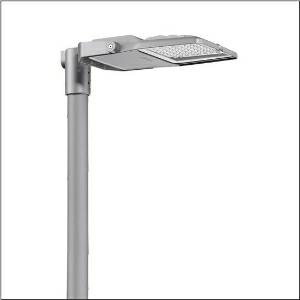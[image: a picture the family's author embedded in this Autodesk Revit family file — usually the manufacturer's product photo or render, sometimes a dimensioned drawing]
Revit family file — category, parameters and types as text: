
# Revit family: floodlight_fl_21_iq_mini___pl64_5xa7771c2e3a_b06c
name_source: partatom
category: Lighting Fixtures
units: mm (PartAtom-declared; Revit-internal decimal feet)

## family parameters
Cut with Voids When Loaded = No
Host = Face
Light Source = No
Part Type = Normal
Room Calculation Point = No
Round Connector Dimension = Use Diameter
Shared = No

## types (1)
- --- (1 x LED, 11790 lm, 87.2 W, 3000K)
    Apparent Load = 87 VA
    CIE Flux Codes = 28 80 98 100 100
    Color Rendering = 70
    Color Temperature = 3000K
    Default Elevation = 1800 mm
    Description = Floodlight FL 21 iQ mini, floodlight, primary light control with lens, of PMMA, primary optical cover: protective disc, of toughened safety glass, transparent, light distribution: PL64, light emission: direct distribution, installation type: surface-mounted, LED, High Power LED, rated luminous flux: 11.790lm, luminous efficacy: 135lm/W, light colour: 730, colour temperature: 3000K, control gear: iQ Comfort/DALI, control: Auto-Match, Temp-Guard, Lumen-Switch, Night-Set, Smart-Wire, Light-Fading, Desk-Remote (wireless, voltage-free reading and setting of iQ features in the workshop via application-optimized NFC function/RFID function), optimised constant luminous flux control (CLO 2.0), with terminal, 6-pole, mains connection: 220..240V, AC, 50/60Hz, start of lifetime: 87W, end of service life: 92W, reduction: 40W, luminaire housing, of diecast aluminium, powder-coated, Siteco® metallic grey (DB 702S), corrosivity category C5 mid according to DIN EN ISO 12944, suitable for swimming pools, chlorine-resistant, sealing non-destructively replaceable, please order mast flange separately, mast bracket, of steel, galvanised, powder-coated, Siteco® metallic grey (DB 702S), protection rating (complete): IP66, insulation class (complete): insulation class II (safety insulation), certification: CE, ENEC, VDE, protection symbol: D, impact resistance: IK08, permissible operating ambient temperature: -40..+40°C, permissible operating ambient temperature for outdoor applications: -40..+50°C, standard: DIN EN 12944, LABS conformity tested according to VDMA 24364:2018-05, packaging unit: 1 piece

Light Distribution: PL64
    Height = 70 mm
    Lamp = 1 x LED
    Lamp Light Flux = 11790 lm
    Lamp Power = 87.2 W
    Lamp count = 1
    Length = 485 mm
    Luminous efficacy = 135 lm/W
    Manufacturer = Siteco
    ModVariant = No
    Model = 5XA7771C2E3A
    Number of Poles = 1
    OnlyDefault = Yes
    Power Factor = 1
    Product Name = Floodlight FL 21 iQ mini | PL64
    Product group = floodlight | pylon annexe
    ProductGroupID = 6200
    Protection Class = Protection class II
    Protection Degree = IP 66
    RLX_Detail_Level = 1
    RLX_Emergency_Light_Flux = 0 lm
    RLX_Emergency_Type = 0
    RLX_Emergency_Type_DB = No
    RlxData = <blob elided: 101413 chars, md5=b12cdf87>
    Socket = socket
    Standby Power = 0 W
    System Light Flux = 11790 lm
    System Power = 87 W
    Type Comments = factory setting: luminous flux: 100 % | dim-lin: 254 | 456 mA
    Type Image = l_1007125.jpg
    URL = http://relux.com
    VarID = @adj_166614
    Voltage = 0 V
    Weight = 0.00 kg
    Width = 337 mm

## geometry (parser evidence)
native form markers: Blend x4, Sweep x12
no freeform markers — native parametric forms only
